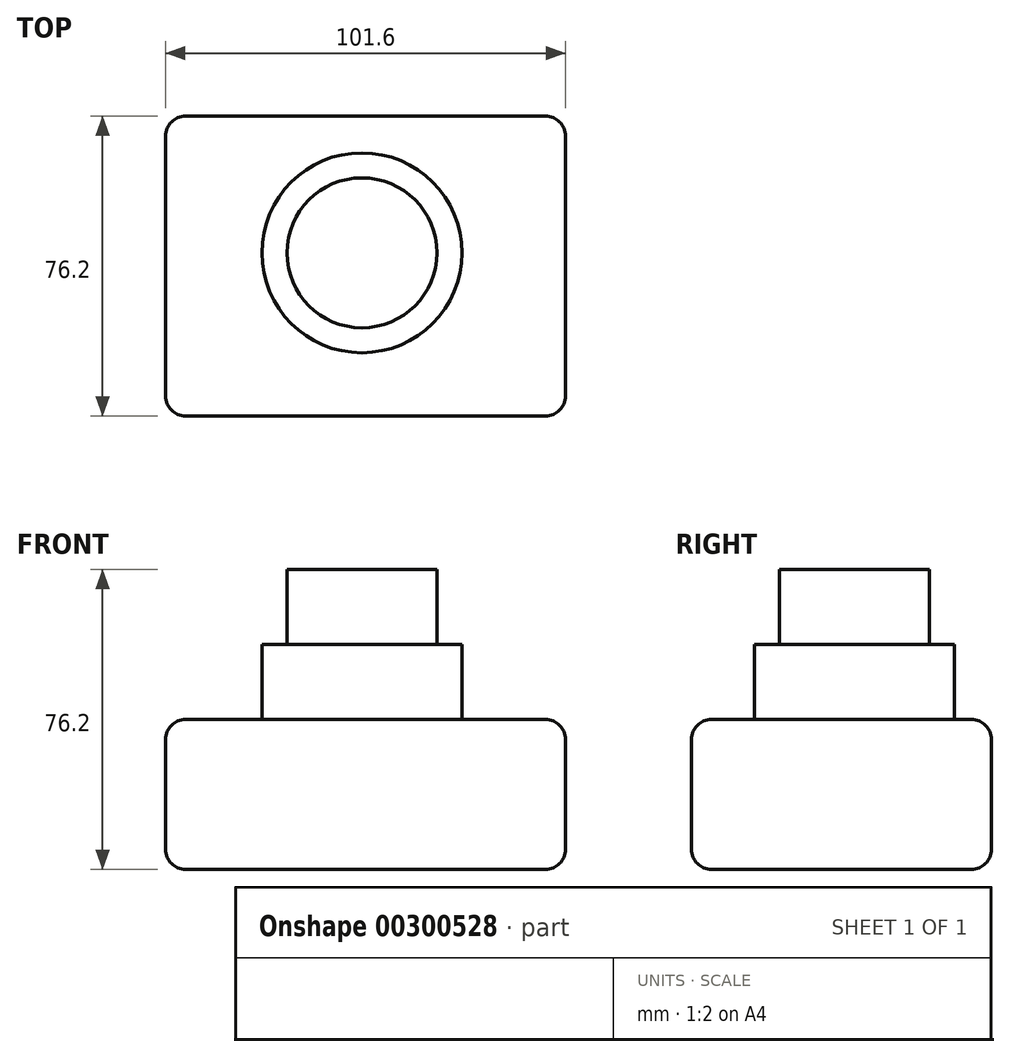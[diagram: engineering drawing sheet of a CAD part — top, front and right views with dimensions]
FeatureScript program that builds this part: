
annotation { "Feature Type Name" : "Feature", "Feature Type Description" : "" }
export const myFeature = defineFeature(function(context is Context, id is Id, definition is map)
    precondition{}
    {
        {
            var Q0;
            Q0=qCreatedBy(makeId("Top.planeOp"),FACE);
            var sketch = newSketch(context, id + "F0", { "sketchPlane" : qUnion([Q0])});
            skLineSegment(sketch, "E0.bottom", {"start": v(-35.37, 34.74) * mm, "end": v(66.23, 34.74) * mm});
            skLineSegment(sketch, "E0.top", {"start": v(-35.37, -41.46) * mm, "end": v(66.23, -41.46) * mm});
            skLineSegment(sketch, "E0.left", {"start": v(-35.37, 34.74) * mm, "end": v(-35.37, -41.46) * mm});
            skLineSegment(sketch, "E0.right", {"start": v(66.23, 34.74) * mm, "end": v(66.23, -41.46) * mm});
            skSolve(sketch);
        }
        {
            var Q0;
            Q0=makeQuery(id+"F0.imprint","IMPRINT",FACE,{"disambiguationData":[TD([[makeQuery(id+"F0.imprint","IMPRINT",EDGE,{"derivedFrom":sQuery(id+"F0.wireOp",EDGE,"E0.bottom")}),-1.0]])]});
            extrude(context, id + "F1", {"entities" : qUnion([Q0]), "depth" : 38.1 * mm});
        }
        {
            var Q0;
            Q0=makeQuery(id+"F1.opExtrude","CAP_FACE",FACE,{"disambiguationData":[OSD([sQuery(id+"F0.wireOp",EDGE,"E0.bottom"),sQuery(id+"F0.wireOp",EDGE,"E0.top"),sQuery(id+"F0.wireOp",EDGE,"E0.left"),sQuery(id+"F0.wireOp",EDGE,"E0.right")])],"isStart":false});
            var sketch = newSketch(context, id + "F2", { "sketchPlane" : qUnion([Q0])});
            skCircle(sketch, "E1", {"center": v(14.5, 0) * mm, "radius": 25.4 * mm});
            skSolve(sketch);
        }
        {
            var Q0;
            Q0=makeQuery(id+"F2.imprint","IMPRINT",FACE,{"disambiguationData":[TD([[makeQuery(id+"F2.imprint","IMPRINT",EDGE,{"derivedFrom":sQuery(id+"F2.wireOp",EDGE,"E1")}),1.0]])]});
            extrude(context, id + "F3", {"entities" : qUnion([Q0]), "operationType" : NewBodyOperationType.ADD, "depth" : 19.05 * mm});
        }
        {
            var Q0;
            Q0=makeQuery(id+"F3.opExtrude","CAP_FACE",FACE,{"disambiguationData":[OSD([sQuery(id+"F2.wireOp",EDGE,"E1")])],"isStart":false});
            var sketch = newSketch(context, id + "F4", { "sketchPlane" : qUnion([Q0])});
            skCircle(sketch, "E2", {"center": v(14.5, 0) * mm, "radius": 19.05 * mm});
            skSolve(sketch);
        }
        {
            var Q0;
            Q0=makeQuery(id+"F4.imprint","IMPRINT",FACE,{"disambiguationData":[TD([[makeQuery(id+"F4.imprint","IMPRINT",EDGE,{"derivedFrom":sQuery(id+"F4.wireOp",EDGE,"E2")}),1.0]])]});
            extrude(context, id + "F5", {"entities" : qUnion([Q0]), "operationType" : NewBodyOperationType.ADD, "depth" : 19.05 * mm});
        }
        {
            var Q0;
            Q0=makeQuery(id+"F1.opExtrude","CAP_EDGE",EDGE,{"disambiguationData":[OSD([sQuery(id+"F0.wireOp",EDGE,"E0.bottom")])],"isStart":false});
            var Q1;
            Q1=makeQuery(id+"F1.opExtrude","SWEPT_EDGE",EDGE,{"disambiguationData":[OSD([sQuery(id+"F0.wireOp",EDGE,"E0.bottom"),sQuery(id+"F0.wireOp",EDGE,"E0.right")])]});
            var Q2;
            Q2=makeQuery(id+"F1.opExtrude","CAP_EDGE",EDGE,{"disambiguationData":[OSD([sQuery(id+"F0.wireOp",EDGE,"E0.bottom")])],"isStart":true});
            var Q3;
            Q3=makeQuery(id+"F1.opExtrude","SWEPT_EDGE",EDGE,{"disambiguationData":[OSD([sQuery(id+"F0.wireOp",EDGE,"E0.bottom"),sQuery(id+"F0.wireOp",EDGE,"E0.left")])]});
            var Q4;
            Q4=makeQuery(id+"F1.opExtrude","CAP_EDGE",EDGE,{"disambiguationData":[OSD([sQuery(id+"F0.wireOp",EDGE,"E0.right")])],"isStart":false});
            var Q5;
            Q5=makeQuery(id+"F1.opExtrude","CAP_EDGE",EDGE,{"disambiguationData":[OSD([sQuery(id+"F0.wireOp",EDGE,"E0.right")])],"isStart":true});
            var Q6;
            Q6=makeQuery(id+"F1.opExtrude","SWEPT_EDGE",EDGE,{"disambiguationData":[OSD([sQuery(id+"F0.wireOp",EDGE,"E0.top"),sQuery(id+"F0.wireOp",EDGE,"E0.right")])]});
            var Q7;
            Q7=makeQuery(id+"F1.opExtrude","CAP_EDGE",EDGE,{"disambiguationData":[OSD([sQuery(id+"F0.wireOp",EDGE,"E0.top")])],"isStart":false});
            var Q8;
            Q8=makeQuery(id+"F1.opExtrude","CAP_EDGE",EDGE,{"disambiguationData":[OSD([sQuery(id+"F0.wireOp",EDGE,"E0.left")])],"isStart":false});
            var Q9;
            Q9=makeQuery(id+"F1.opExtrude","CAP_EDGE",EDGE,{"disambiguationData":[OSD([sQuery(id+"F0.wireOp",EDGE,"E0.top")])],"isStart":true});
            var Q10;
            Q10=makeQuery(id+"F1.opExtrude","CAP_EDGE",EDGE,{"disambiguationData":[OSD([sQuery(id+"F0.wireOp",EDGE,"E0.left")])],"isStart":true});
            var Q11;
            Q11=makeQuery(id+"F1.opExtrude","SWEPT_EDGE",EDGE,{"disambiguationData":[OSD([sQuery(id+"F0.wireOp",EDGE,"E0.top"),sQuery(id+"F0.wireOp",EDGE,"E0.left")])]});
            fillet(context, id + "F6", {"entities" : qUnion([Q0, Q1, Q2, Q3, Q4, Q5, Q6, Q7, Q8, Q9, Q10, Q11]), "radius" : 5.08 * mm, "tangentPropagation" : true, "allowEdgeOverflow" : false});
        }
    });
